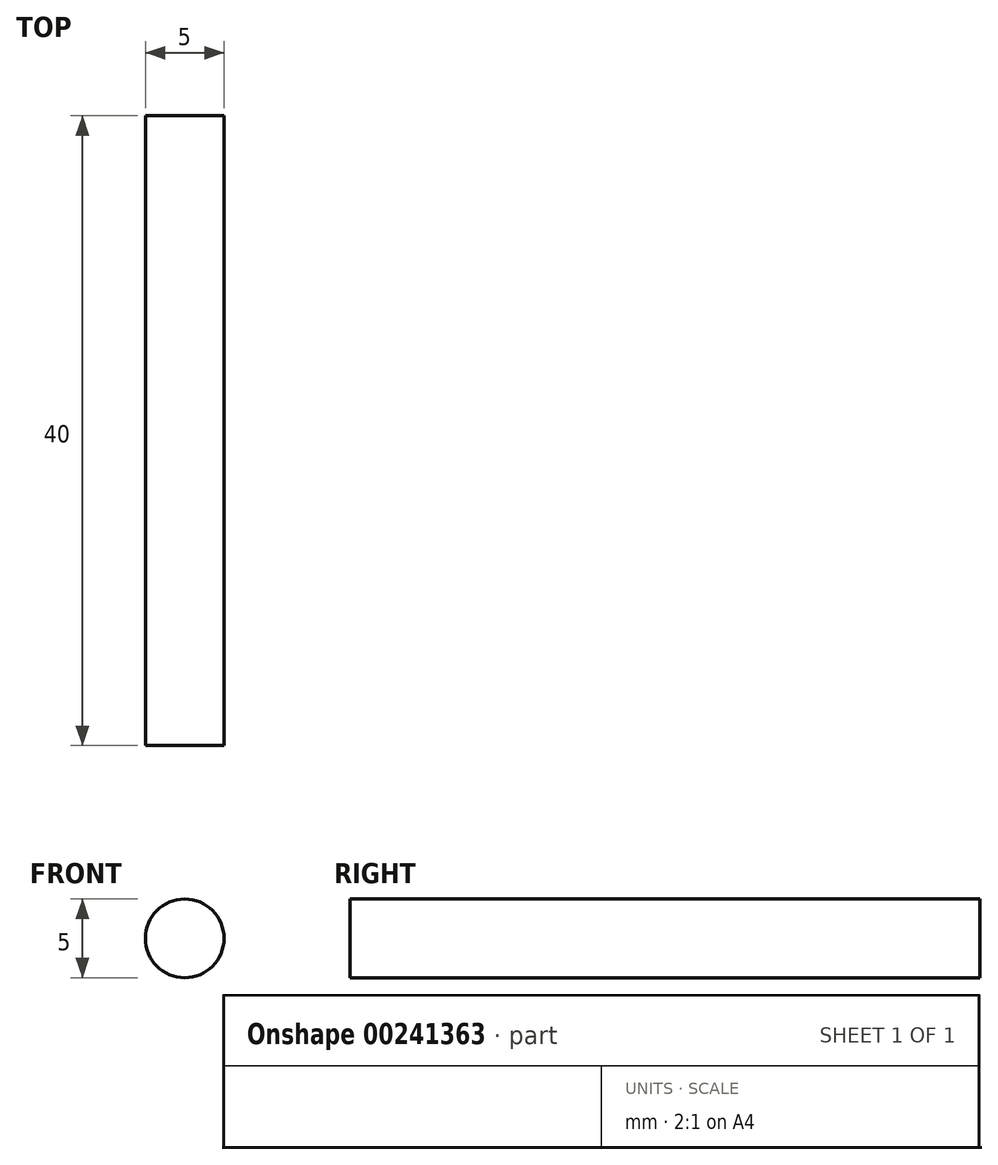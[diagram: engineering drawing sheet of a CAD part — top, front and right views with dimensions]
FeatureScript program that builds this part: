
annotation { "Feature Type Name" : "Feature", "Feature Type Description" : "" }
export const myFeature = defineFeature(function(context is Context, id is Id, definition is map)
    precondition{}
    {
        {
            var Q0;
            Q0=qCreatedBy(makeId("Front.planeOp"),FACE);
            var sketch = newSketch(context, id + "F0", { "sketchPlane" : qUnion([Q0])});
            skCircle(sketch, "E0", {"center": v(0, 0) * mm, "radius": 2.5 * mm});
            skSolve(sketch);
        }
        {
            var Q0;
            Q0 = qSketchRegion(id + "F0", true);
            extrude(context, id + "F1", {"entities" : qUnion([Q0]), "depth" : 40 * mm});
        }
    });
